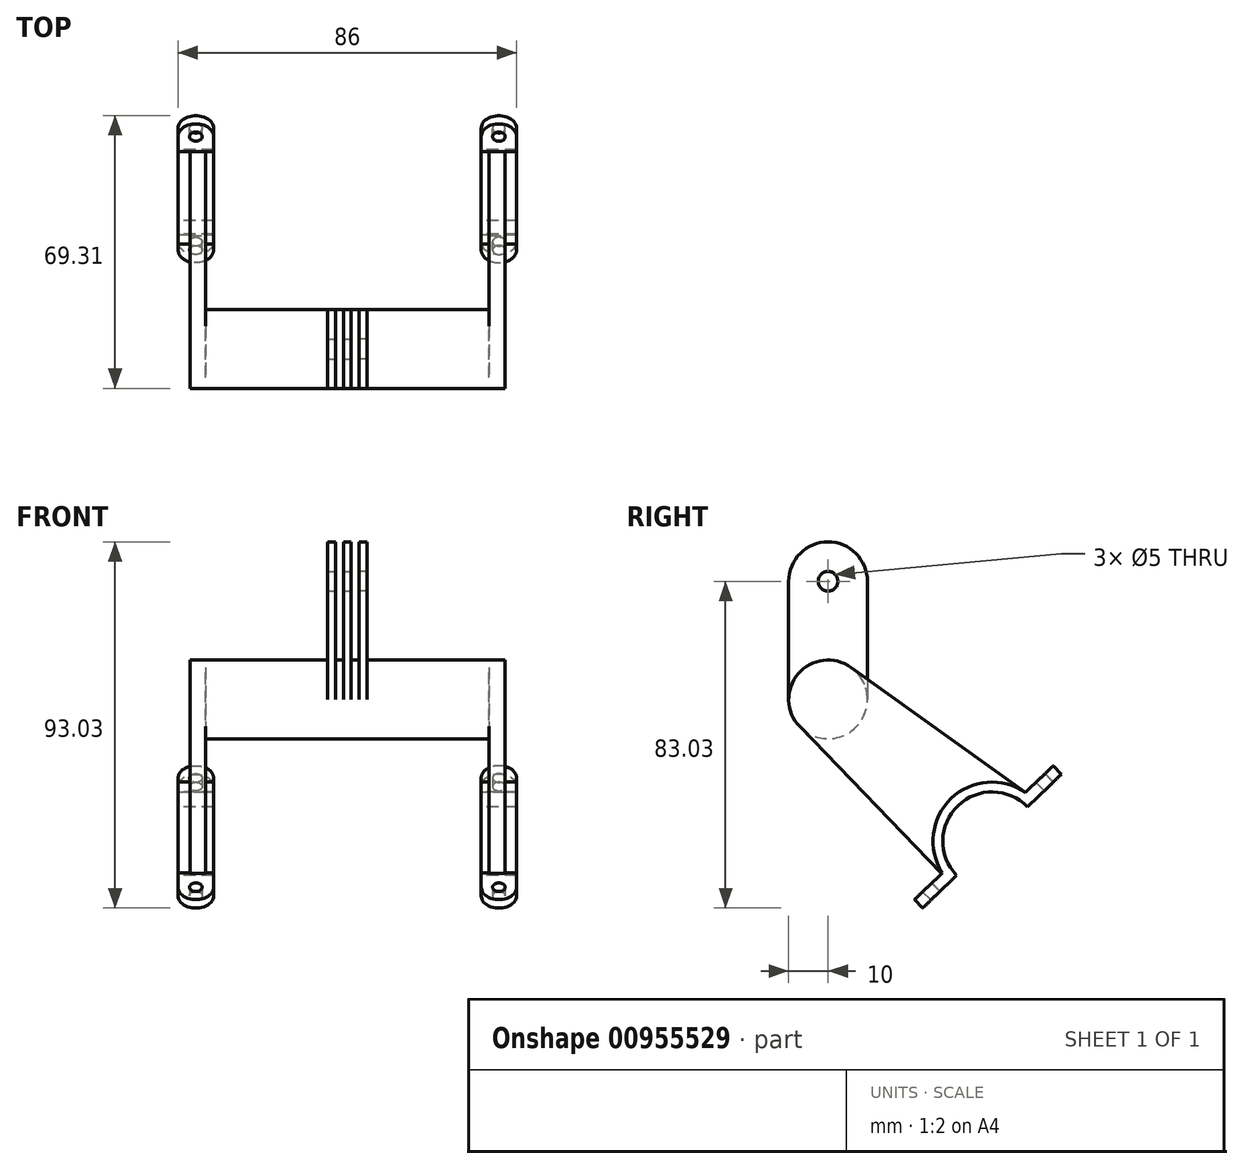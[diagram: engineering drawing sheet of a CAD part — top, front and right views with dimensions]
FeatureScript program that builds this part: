
annotation { "Feature Type Name" : "Feature", "Feature Type Description" : "" }
export const myFeature = defineFeature(function(context is Context, id is Id, definition is map)
    precondition{}
    {
        {
            var Q0;
            Q0=qCreatedBy(makeId("Top.planeOp"),FACE);
            var sketch = newSketch(context, id + "F0", { "sketchPlane" : qUnion([Q0])});
            skLineSegment(sketch, "E0.bottom", {"start": v(0, 20) * mm, "end": v(-40, 20) * mm});
            skLineSegment(sketch, "E0.top", {"start": v(0, 0) * mm, "end": v(-40, 0) * mm});
            skLineSegment(sketch, "E0.left", {"start": v(0, 20) * mm, "end": v(0, 0) * mm});
            skLineSegment(sketch, "E0.right", {"start": v(-40, 20) * mm, "end": v(-40, 0) * mm});
            skLineSegment(sketch, "E1.bottom", {"start": v(0, 20) * mm, "end": v(-1, 20) * mm});
            skLineSegment(sketch, "E1.top", {"start": v(0, 0) * mm, "end": v(-1, 0) * mm});
            skLineSegment(sketch, "E1.right", {"start": v(-1, 20) * mm, "end": v(-1, 0) * mm});
            skLineSegment(sketch, "E2.bottom", {"start": v(-3, 20) * mm, "end": v(-5, 20) * mm});
            skLineSegment(sketch, "E2.top", {"start": v(-3, 0) * mm, "end": v(-5, 0) * mm});
            skLineSegment(sketch, "E2.left", {"start": v(-3, 20) * mm, "end": v(-3, 0) * mm});
            skLineSegment(sketch, "E2.right", {"start": v(-5, 20) * mm, "end": v(-5, 0) * mm});
            skSolve(sketch);
        }
        {
            var Q0;
            {var subQ3=sQuery(id+"F0.wireOp",EDGE,"E2.left");var subQ9=makeQuery(id+"F0.imprint","IMPRINT",EDGE,{"derivedFrom":subQ3});var subQ10=sQuery(id+"F0.wireOp",EDGE,"E1.right");var subQ13=makeQuery(id+"F0.imprint","IMPRINT",EDGE,{"derivedFrom":subQ10});var subQ14=sQuery(id+"F0.wireOp",EDGE,"E0.left");var subQ15=sQuery(id+"F0.wireOp",EDGE,"E0.right");Q0=qUnion([makeQuery(id+"F0.imprint","IMPRINT",FACE,{"disambiguationData":[TD([[makeQuery(id+"F0.imprint","IMPRINT",EDGE,{"derivedFrom":subQ15}),1.0]])]}),makeQuery(id+"F0.imprint","IMPRINT",FACE,{"disambiguationData":[TD([[makeQuery(id+"F0.imprint","IMPRINT",EDGE,{"derivedFrom":subQ14}),-1.0]])]}),makeQuery(id+"F0.imprint","IMPRINT",FACE,{"disambiguationData":[TD([[subQ13,-1.0]])]}),makeQuery(id+"F0.imprint","IMPRINT",FACE,{"disambiguationData":[TD([[subQ9,-1.0]])]})]);}
            extrude(context, id + "F1", {"entities" : qUnion([Q0]), "depth" : 20 * mm, "offsetDistance" : 25 * mm});
        }
        {
            var Q0;
            {var subQ2=sQuery(id+"F0.wireOp",EDGE,"E2.left");Q0=makeQuery(id+"F0.imprint","IMPRINT",FACE,{"disambiguationData":[TD([[makeQuery(id+"F0.imprint","IMPRINT",EDGE,{"derivedFrom":subQ2}),-1.0]])]});}
            var Q1;
            {var subQ2=sQuery(id+"F0.wireOp",EDGE,"E0.left");Q1=makeQuery(id+"F0.imprint","IMPRINT",FACE,{"disambiguationData":[TD([[makeQuery(id+"F0.imprint","IMPRINT",EDGE,{"derivedFrom":subQ2}),-1.0]])]});}
            extrude(context, id + "F2", {"entities" : qUnion([Q0, Q1]), "operationType" : NewBodyOperationType.ADD, "depth" : 50 * mm, "offsetDistance" : 25 * mm});
        }
        {
            var Q0;
            {var subQ0=sQuery(id+"F0.wireOp",EDGE,"E0.right");var subQ1=sQuery(id+"F0.wireOp",EDGE,"E0.top");Q0=makeQuery(id+"F2.boolean.opBoolean","SPLIT",EDGE,{"disambiguationData":[TD([makeQuery(id+"F1.opExtrude","SWEPT_FACE",FACE,{"disambiguationData":[OSD([subQ0])]})])],"derivedFrom":makeQuery(id+"F1.opExtrude","CAP_EDGE",EDGE,{"disambiguationData":[OSD([subQ1])],"isStart":false})});}
            var Q1;
            {var subQ1=sQuery(id+"F0.wireOp",EDGE,"E0.bottom");var subQ2=sQuery(id+"F0.wireOp",EDGE,"E0.right");Q1=makeQuery(id+"F2.boolean.opBoolean","SPLIT",EDGE,{"disambiguationData":[TD([makeQuery(id+"F1.opExtrude","SWEPT_FACE",FACE,{"disambiguationData":[OSD([subQ2])]})])],"derivedFrom":makeQuery(id+"F1.opExtrude","CAP_EDGE",EDGE,{"disambiguationData":[OSD([subQ1])],"isStart":false})});}
            var Q2;
            Q2=makeQuery(id+"F1.opExtrude","CAP_EDGE",EDGE,{"disambiguationData":[OSD([sQuery(id+"F0.wireOp",EDGE,"E0.top")])],"isStart":true});
            var Q3;
            Q3=makeQuery(id+"F1.opExtrude","CAP_EDGE",EDGE,{"disambiguationData":[OSD([sQuery(id+"F0.wireOp",EDGE,"E0.bottom")])],"isStart":true});
            var Q4;
            {var subQ0=sQuery(id+"F0.wireOp",EDGE,"E1.right");var subQ1=sQuery(id+"F0.wireOp",EDGE,"E0.top");Q4=makeQuery(id+"F2.boolean.opBoolean","SPLIT",EDGE,{"disambiguationData":[TD([makeQuery(id+"F2.opExtrude","SWEPT_FACE",FACE,{"disambiguationData":[OSD([subQ0])]})])],"derivedFrom":makeQuery(id+"F1.opExtrude","CAP_EDGE",EDGE,{"disambiguationData":[OSD([subQ1])],"isStart":false})});}
            var Q5;
            {var subQ0=sQuery(id+"F0.wireOp",EDGE,"E1.right");var subQ1=sQuery(id+"F0.wireOp",EDGE,"E0.bottom");Q5=makeQuery(id+"F2.boolean.opBoolean","SPLIT",EDGE,{"disambiguationData":[TD([makeQuery(id+"F2.opExtrude","SWEPT_FACE",FACE,{"disambiguationData":[OSD([subQ0])]})])],"derivedFrom":makeQuery(id+"F1.opExtrude","CAP_EDGE",EDGE,{"disambiguationData":[OSD([subQ1])],"isStart":false})});}
            var Q6;
            {var subQ0=sQuery(id+"F0.wireOp",EDGE,"E0.top");Q6=makeQuery(id+"F2.opExtrude","CAP_EDGE",EDGE,{"disambiguationData":[OSD([subQ0]),TDD([makeQuery(id+"F0.imprint","IMPRINT",EDGE,{"disambiguationData":[TD([[makeQuery(id+"F0.imprint","INTERSECT",VERTEX,{"derivedFrom":[subQ0,sQuery(id+"F0.wireOp",EDGE,"E2.right")]}),1.0]])],"derivedFrom":subQ0})])],"isStart":false});}
            var Q7;
            {var subQ0=sQuery(id+"F0.wireOp",EDGE,"E0.top");Q7=makeQuery(id+"F2.opExtrude","CAP_EDGE",EDGE,{"disambiguationData":[OSD([subQ0]),TDD([makeQuery(id+"F0.imprint","IMPRINT",EDGE,{"disambiguationData":[TD([[makeQuery(id+"F0.imprint","INTERSECT",VERTEX,{"derivedFrom":[subQ0,sQuery(id+"F0.wireOp",EDGE,"E1.right")]}),1.0]])],"derivedFrom":subQ0})])],"isStart":false});}
            var Q8;
            {var subQ0=sQuery(id+"F0.wireOp",EDGE,"E0.bottom");Q8=makeQuery(id+"F2.opExtrude","CAP_EDGE",EDGE,{"disambiguationData":[OSD([subQ0]),TDD([makeQuery(id+"F0.imprint","IMPRINT",EDGE,{"disambiguationData":[TD([[makeQuery(id+"F0.imprint","INTERSECT",VERTEX,{"derivedFrom":[subQ0,sQuery(id+"F0.wireOp",EDGE,"E2.right")]}),1.0]])],"derivedFrom":subQ0})])],"isStart":false});}
            var Q9;
            {var subQ0=sQuery(id+"F0.wireOp",EDGE,"E0.bottom");Q9=makeQuery(id+"F2.opExtrude","CAP_EDGE",EDGE,{"disambiguationData":[OSD([subQ0]),TDD([makeQuery(id+"F0.imprint","IMPRINT",EDGE,{"disambiguationData":[TD([[makeQuery(id+"F0.imprint","INTERSECT",VERTEX,{"derivedFrom":[subQ0,sQuery(id+"F0.wireOp",EDGE,"E1.right")]}),1.0]])],"derivedFrom":subQ0})])],"isStart":false});}
            fillet(context, id + "F3", {"entities" : qUnion([Q0, Q1, Q2, Q3, Q4, Q5, Q6, Q7, Q8, Q9]), "radius" : 10 * mm, "tangentPropagation" : true, "allowEdgeOverflow" : false});
        }
        {
            var Q0;
            {var subQ0=sQuery(id+"F0.wireOp",EDGE,"E0.left");Q0=makeQuery(id+"F2.boolean.opBoolean","MERGE",FACE,{"derivedFrom":[makeQuery(id+"F1.opExtrude","SWEPT_FACE",FACE,{"disambiguationData":[OSD([subQ0])]}),makeQuery(id+"F2.opExtrude","SWEPT_FACE",FACE,{"disambiguationData":[OSD([subQ0])]})]});}
            var sketch = newSketch(context, id + "F4", { "sketchPlane" : qUnion([Q0])});
            skPoint(sketch, "E3", {"position": v(10, 40) * mm});
            skSolve(sketch);
        }
        {
            var Q0;
            Q0=sQuery(id+"F4.wireOp",VERTEX,"E3");
            var Q1;
            Q1=makeQuery(id+"F1.opExtrude","SWEPT_BODY",BODY,{"disambiguationData":[OSD([sQuery(id+"F0.wireOp",EDGE,"E0.bottom"),sQuery(id+"F0.wireOp",EDGE,"E0.top"),sQuery(id+"F0.wireOp",EDGE,"E0.left"),sQuery(id+"F0.wireOp",EDGE,"E0.right")])]});
            hole(context, id + "F5", {"style" : HoleStyle.SIMPLE, "endStyle" : HoleEndStyle.THROUGH, "holeDiameter" : 5 * mm, "majorDiameter" : 5 * mm, "isTappedThrough" : true, "tappedDepth" : 12 * mm, "tapClearance" : 3, "locations" : qUnion([Q0]), "scope" : qUnion([Q1])});
        }
        {
            var Q0;
            Q0=makeQuery(id+"F1.opExtrude","SWEPT_FACE",FACE,{"disambiguationData":[OSD([sQuery(id+"F0.wireOp",EDGE,"E0.right")])]});
            var sketch = newSketch(context, id + "F6", { "sketchPlane" : qUnion([Q0])});
            skArc(sketch, "E4", {"start": v(-40.87, -36.43) * mm, "mid": v(-41.26, -15.22) * mm, "end": v(-62.47, -15.61) * mm});
            skArc(sketch, "E5", {"start": v(-42.67, -34.7) * mm, "mid": v(-43, -17.02) * mm, "end": v(-60.67, -17.35) * mm});
            skLineSegment(sketch, "E6", {"start": v(-40.87, -36.43) * mm, "end": v(-2.8, 3.06) * mm});
            skLineSegment(sketch, "E7", {"start": v(-15.83, 18.13) * mm, "end": v(-60.4, -13.83) * mm});
            skLineSegment(sketch, "E8", {"start": v(-40.87, -36.43) * mm, "end": v(-42.67, -34.7) * mm});
            skLineSegment(sketch, "E9.trimOffspring", {"start": v(-60.67, -17.35) * mm, "end": v(-62.47, -15.61) * mm});
            skPoint(sketch, "E10", {"position": v(-10, 10) * mm});
            skSolve(sketch);
        }
        {
            var Q0;
            {var subQ0=sQuery(id+"F6.wireOp",EDGE,"E6");Q0=makeQuery(id+"F6.imprint","IMPRINT",FACE,{"disambiguationData":[TD([[makeQuery(id+"F6.imprint","IMPRINT",EDGE,{"derivedFrom":subQ0}),1.0]])]});}
            extrude(context, id + "F7", {"entities" : qUnion([Q0]), "operationType" : NewBodyOperationType.ADD, "oppositeDirection" : true, "depth" : 4 * mm, "offsetDistance" : 25 * mm});
        }
        {
            var Q0;
            Q0 = qSketchRegion(id + "F6", true);
            extrude(context, id + "F8", {"entities" : qUnion([Q0]), "depth" : 3 * mm, "offsetDistance" : 25 * mm});
        }
        {
            var Q0;
            Q0 = qSketchRegion(id + "F6", true);
            extrude(context, id + "F9", {"entities" : qUnion([Q0]), "oppositeDirection" : true, "depth" : 6 * mm, "offsetDistance" : 25 * mm});
        }
        {
            var Q0;
            Q0=makeQuery(id+"F9.opExtrude","SWEPT_FACE",FACE,{"disambiguationData":[OSD([sQuery(id+"F6.wireOp",EDGE,"E9.trimOffspring")])]});
            var sketch = newSketch(context, id + "F10", { "sketchPlane" : qUnion([Q0])});
            skLineSegment(sketch, "E11.bottom", {"start": v(-43, -31.64) * mm, "end": v(-34, -31.64) * mm});
            skLineSegment(sketch, "E11.top", {"start": v(-38.5, -43.64) * mm, "end": v(-38.5, -43.64) * mm});
            skLineSegment(sketch, "E11.left", {"start": v(-43, -31.64) * mm, "end": v(-43, -39.14) * mm});
            skLineSegment(sketch, "E11.right", {"start": v(-34, -31.64) * mm, "end": v(-34, -39.14) * mm});
            skPoint(sketch, "E12.visualSharp", {"position": v(-34, -43.64) * mm});
            skArc(sketch, "E12.filletArc", {"start": v(-38.5, -43.64) * mm, "mid": v(-35.32, -42.32) * mm, "end": v(-34, -39.14) * mm});
            skPoint(sketch, "E13.visualSharp", {"position": v(-43, -43.64) * mm});
            skArc(sketch, "E13.filletArc", {"start": v(-43, -39.14) * mm, "mid": v(-41.68, -42.32) * mm, "end": v(-38.5, -43.64) * mm});
            skPoint(sketch, "E14", {"position": v(-38.5, -31.64) * mm});
            skPoint(sketch, "E15", {"position": v(-38.5, -19.14) * mm});
            skLineSegment(sketch, "E16.1.0", {"start": v(-34, -6.64) * mm, "end": v(-34, 0.86) * mm});
            skLineSegment(sketch, "E16.1.1", {"start": v(-34, -6.64) * mm, "end": v(-43, -6.64) * mm});
            skLineSegment(sketch, "E16.1.2", {"start": v(-43, -6.64) * mm, "end": v(-43, 0.86) * mm});
            skArc(sketch, "E16.1.3", {"start": v(-38.5, 5.36) * mm, "mid": v(-41.68, 4.04) * mm, "end": v(-43, 0.86) * mm});
            skArc(sketch, "E16.1.4", {"start": v(-34, 0.86) * mm, "mid": v(-35.32, 4.04) * mm, "end": v(-38.5, 5.36) * mm});
            skSolve(sketch);
        }
        {
            var Q0;
            {var subQ4=sQuery(id+"F10.wireOp",EDGE,"E11.left");Q0=makeQuery(id+"F10.imprint","IMPRINT",FACE,{"disambiguationData":[TD([[makeQuery(id+"F10.imprint","IMPRINT",EDGE,{"derivedFrom":subQ4}),1.0]])]});}
            var Q1;
            {var subQ1=sQuery(id+"F6.wireOp",EDGE,"E9.trimOffspring");var subQ2=makeQuery(id+"F9.opExtrude","CAP_EDGE",EDGE,{"disambiguationData":[OSD([subQ1])],"isStart":true});Q1=makeQuery(id+"F10.imprint","IMPRINT",FACE,{"disambiguationData":[TD([[makeQuery(id+"F10.imprint","IMPRINT",EDGE,{"derivedFrom":subQ2}),1.0]])]});}
            extrude(context, id + "F11", {"entities" : qUnion([Q0, Q1]), "oppositeDirection" : true, "depth" : 3 * mm, "offsetDistance" : 25 * mm});
        }
        {
            var Q0;
            Q0=sQuery(id+"F10.wireOp",VERTEX,"E12.filletArc.center");
            var Q1;
            Q1=makeQuery(id+"F11.opExtrude","SWEPT_BODY",BODY,{"disambiguationData":[OSD([sQuery(id+"F10.wireOp",EDGE,"E11.bottom"),sQuery(id+"F10.wireOp",EDGE,"E11.left"),sQuery(id+"F10.wireOp",EDGE,"E11.right"),sQuery(id+"F10.wireOp",EDGE,"E12.filletArc"),sQuery(id+"F10.wireOp",EDGE,"E13.filletArc")])]});
            hole(context, id + "F12", {"style" : HoleStyle.SIMPLE, "endStyle" : HoleEndStyle.THROUGH, "holeDiameter" : 3.2 * mm, "majorDiameter" : 5 * mm, "isTappedThrough" : true, "tappedDepth" : 12 * mm, "tapClearance" : 3, "locations" : qUnion([Q0]), "scope" : qUnion([Q1])});
        }
        {
            var Q0;
            Q0=makeQuery(id+"F10.imprint","IMPRINT",FACE,{"disambiguationData":[TD([[makeQuery(id+"F10.imprint","IMPRINT",EDGE,{"derivedFrom":sQuery(id+"F10.wireOp",EDGE,"E16.1.0")}),1.0]])]});
            extrude(context, id + "F13", {"entities" : qUnion([Q0]), "oppositeDirection" : true, "depth" : 3 * mm, "offsetDistance" : 25 * mm});
        }
        {
            var Q0;
            Q0=sQuery(id+"F10.wireOp",VERTEX,"E16.1.3.center");
            var Q1;
            Q1=makeQuery(id+"F13.opExtrude","SWEPT_BODY",BODY,{"disambiguationData":[OSD([sQuery(id+"F10.wireOp",EDGE,"E16.1.0"),sQuery(id+"F10.wireOp",EDGE,"E16.1.1"),sQuery(id+"F10.wireOp",EDGE,"E16.1.2"),sQuery(id+"F10.wireOp",EDGE,"E16.1.3"),sQuery(id+"F10.wireOp",EDGE,"E16.1.4")])]});
            hole(context, id + "F14", {"style" : HoleStyle.SIMPLE, "endStyle" : HoleEndStyle.THROUGH, "holeDiameter" : 3.2 * mm, "majorDiameter" : 5 * mm, "isTappedThrough" : true, "tappedDepth" : 12 * mm, "tapClearance" : 3, "locations" : qUnion([Q0]), "scope" : qUnion([Q1])});
        }
        {
            var Q0;
            Q0=makeQuery(id+"F1.opExtrude","SWEPT_BODY",BODY,{"disambiguationData":[OSD([sQuery(id+"F0.wireOp",EDGE,"E0.bottom"),sQuery(id+"F0.wireOp",EDGE,"E0.top"),sQuery(id+"F0.wireOp",EDGE,"E0.left"),sQuery(id+"F0.wireOp",EDGE,"E0.right")])]});
            var Q1;
            Q1=makeQuery(id+"F9.opExtrude","SWEPT_BODY",BODY,{"disambiguationData":[OSD([sQuery(id+"F6.wireOp",EDGE,"E4"),sQuery(id+"F6.wireOp",EDGE,"E5"),sQuery(id+"F6.wireOp",EDGE,"E8"),sQuery(id+"F6.wireOp",EDGE,"E9.trimOffspring")])]});
            var Q2;
            Q2=makeQuery(id+"F11.opExtrude","SWEPT_BODY",BODY,{"disambiguationData":[OSD([sQuery(id+"F10.wireOp",EDGE,"E11.bottom"),sQuery(id+"F10.wireOp",EDGE,"E11.left"),sQuery(id+"F10.wireOp",EDGE,"E11.right"),sQuery(id+"F10.wireOp",EDGE,"E12.filletArc"),sQuery(id+"F10.wireOp",EDGE,"E13.filletArc")])]});
            var Q3;
            Q3=makeQuery(id+"F8.opExtrude","SWEPT_BODY",BODY,{"disambiguationData":[OSD([sQuery(id+"F6.wireOp",EDGE,"E4"),sQuery(id+"F6.wireOp",EDGE,"E5"),sQuery(id+"F6.wireOp",EDGE,"E8"),sQuery(id+"F6.wireOp",EDGE,"E9.trimOffspring")])]});
            var Q4;
            Q4=makeQuery(id+"F13.opExtrude","SWEPT_BODY",BODY,{"disambiguationData":[OSD([sQuery(id+"F10.wireOp",EDGE,"E16.1.0"),sQuery(id+"F10.wireOp",EDGE,"E16.1.1"),sQuery(id+"F10.wireOp",EDGE,"E16.1.2"),sQuery(id+"F10.wireOp",EDGE,"E16.1.3"),sQuery(id+"F10.wireOp",EDGE,"E16.1.4")])]});
            var Q5;
            Q5=qCreatedBy(makeId("Right.planeOp"),FACE);
            mirror(context, id + "F15", {"operationType" : NewBodyOperationType.ADD, "entities" : qUnion([Q0, Q1, Q2, Q3, Q4]), "mirrorPlane" : qUnion([Q5])});
        }
    });
